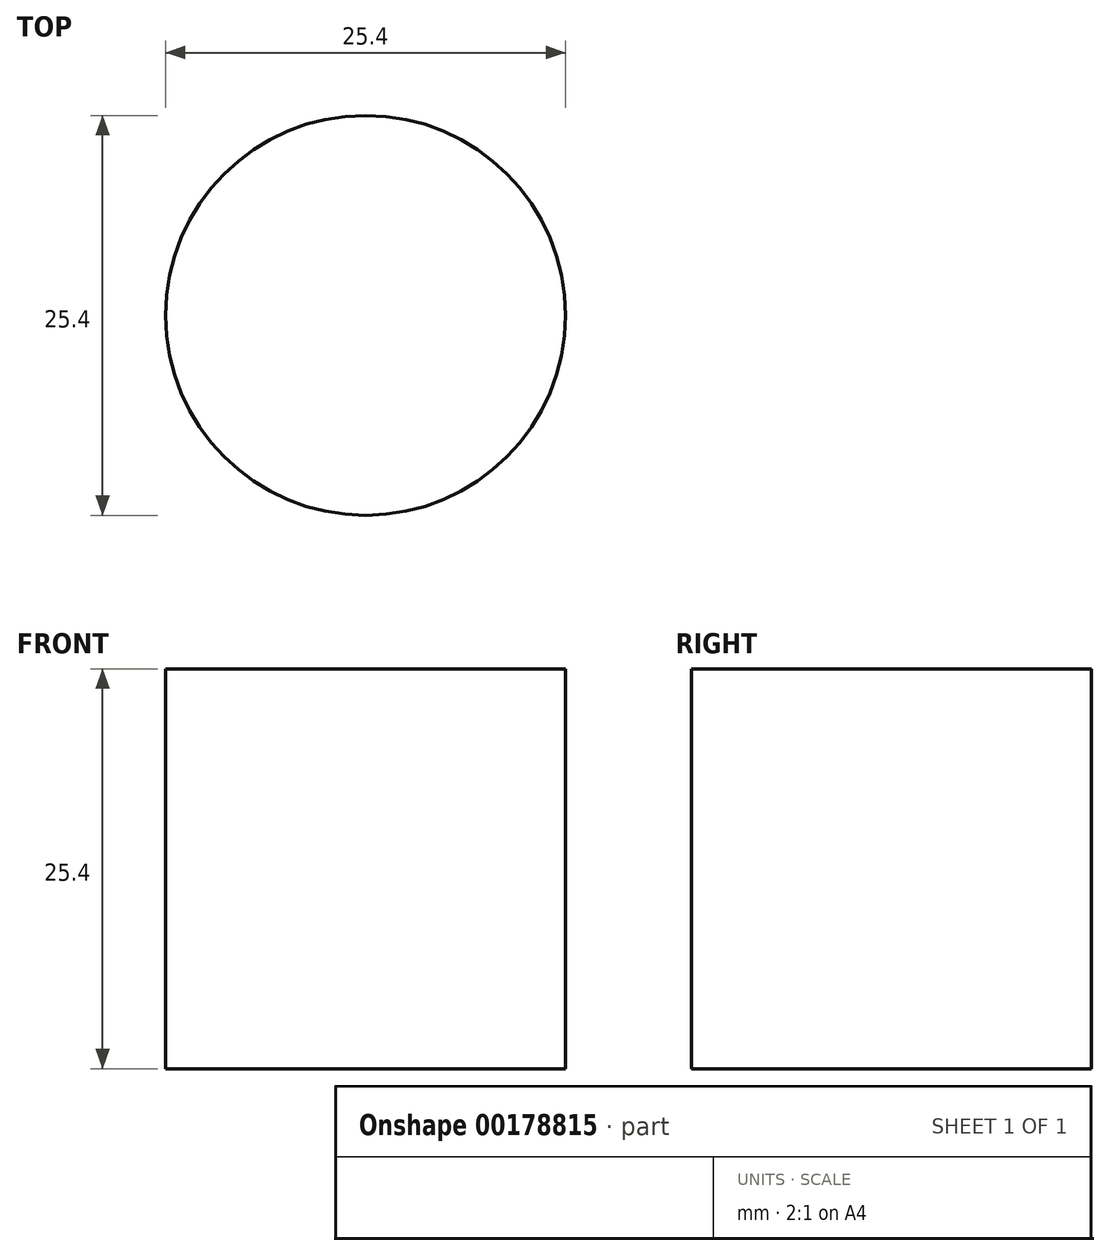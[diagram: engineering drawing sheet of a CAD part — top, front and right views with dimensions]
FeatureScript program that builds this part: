
annotation { "Feature Type Name" : "Feature", "Feature Type Description" : "" }
export const myFeature = defineFeature(function(context is Context, id is Id, definition is map)
    precondition{}
    {
        {
            var Q0;
            Q0=qCreatedBy(makeId("Top.planeOp"),FACE);
            var sketch = newSketch(context, id + "F1", { "sketchPlane" : qUnion([Q0])});
            skCircle(sketch, "E0", {"center": v(0, 0) * mm, "radius": 12.7 * mm});
            skSolve(sketch);
        }
        {
            var Q0;
            Q0 = qSketchRegion(id + "F1", true);
            extrude(context, id + "F0", {"entities" : qUnion([Q0]), "depth" : 25.4 * mm});
        }
    });
